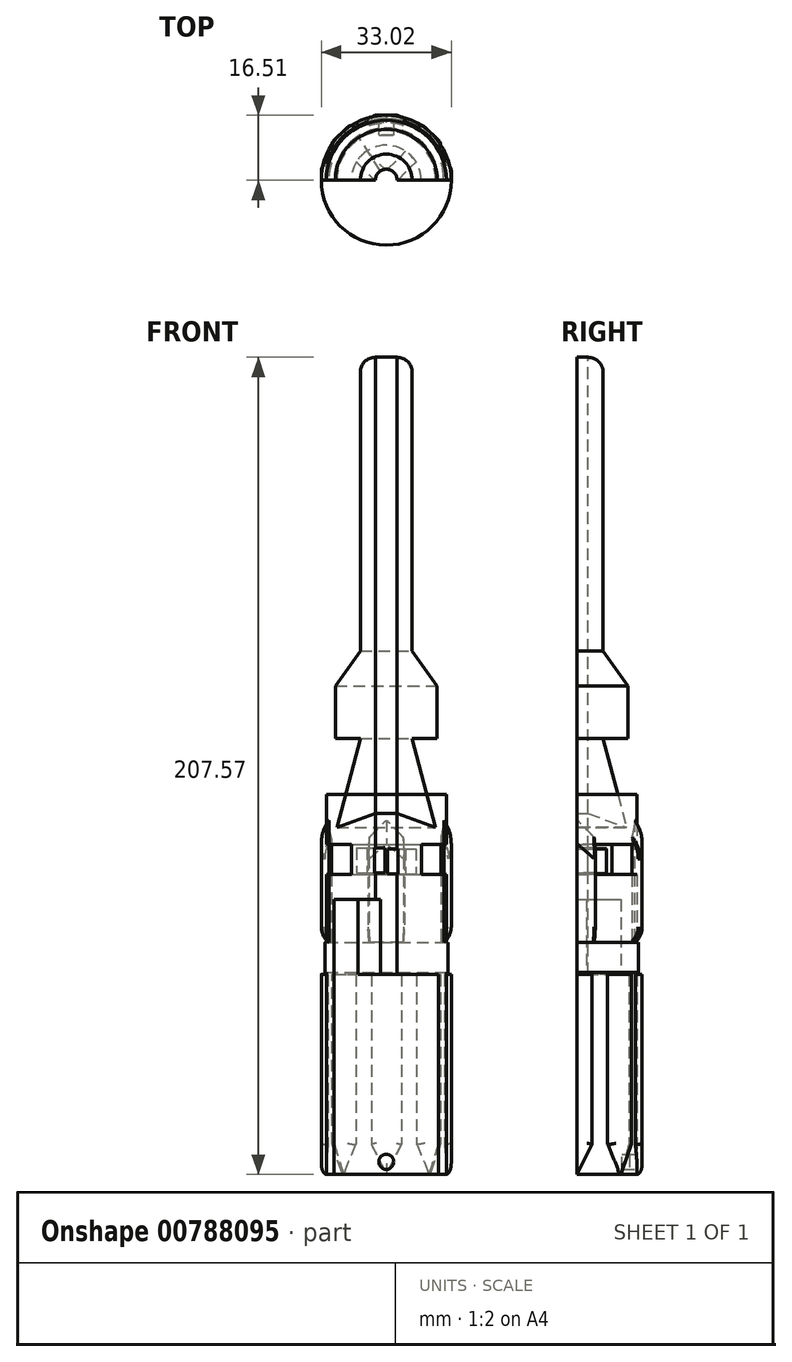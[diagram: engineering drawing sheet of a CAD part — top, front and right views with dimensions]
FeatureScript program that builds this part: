
annotation { "Feature Type Name" : "Feature", "Feature Type Description" : "" }
export const myFeature = defineFeature(function(context is Context, id is Id, definition is map)
    precondition{}
    {
        {
            var Q0;
            Q0=qCreatedBy(makeId("Right.planeOp"),FACE);
            var sketch = newSketch(context, id + "F0", { "sketchPlane" : qUnion([Q0])});
            skLineSegment(sketch, "E0", {"start": v(0, 0) * mm, "end": v(0, 228.6) * mm});
            skLineSegment(sketch, "E1", {"start": v(0, 0) * mm, "end": v(-15.24, 0) * mm});
            skLineSegment(sketch, "E2", {"start": v(-15.24, 0) * mm, "end": v(-15.24, 51.26) * mm});
            skLineSegment(sketch, "E3", {"start": v(-15.24, 76.2) * mm, "end": v(-8.9, 76.2) * mm});
            skLineSegment(sketch, "E4", {"start": v(-8.9, 76.2) * mm, "end": v(-8.9, 83.82) * mm});
            skLineSegment(sketch, "E5", {"start": v(-8.9, 83.82) * mm, "end": v(-15.24, 83.82) * mm});
            skLineSegment(sketch, "E6", {"start": v(-15.24, 83.82) * mm, "end": v(-15.24, 96.52) * mm});
            skLineSegment(sketch, "E7", {"start": v(-15.24, 96.52) * mm, "end": v(-8.9, 96.52) * mm});
            skLineSegment(sketch, "E8", {"start": v(-8.9, 96.52) * mm, "end": v(0, 96.52) * mm});
            skLineSegment(sketch, "E9", {"start": v(-15.24, 51.26) * mm, "end": v(-15.62, 51.26) * mm});
            skLineSegment(sketch, "E10", {"start": v(-15.62, 51.26) * mm, "end": v(-15.62, 58.88) * mm});
            skLineSegment(sketch, "E11", {"start": v(-15.62, 58.88) * mm, "end": v(-15.24, 58.88) * mm});
            skLineSegment(sketch, "E12.trimOffspring", {"start": v(-15.24, 58.88) * mm, "end": v(-15.24, 76.2) * mm});
            skSolve(sketch);
        }
        {
            var Q0;
            {var subQ0=sQuery(id+"F0.wireOp",EDGE,"E1");Q0=makeQuery(id+"F0.imprint","IMPRINT",FACE,{"disambiguationData":[TD([[makeQuery(id+"F0.imprint","IMPRINT",EDGE,{"derivedFrom":subQ0}),-1.0]])]});}
            var Q1;
            Q1=sQuery(id+"F0.wireOp",EDGE,"E0");
            revolve(context, id + "F1", {"surfaceOperationType" : NewSurfaceOperationType.NEW, "entities" : qUnion([Q0]), "axis" : qUnion([Q1]), "revolveType" : RevolveType.FULL});
        }
        {
            var Q0;
            Q0=qCreatedBy(makeId("Front.planeOp"),FACE);
            cPlane(context, id + "F2", {"entities" : qUnion([Q0]), "cplaneType" : CPlaneType.OFFSET, "offset" : 15.24 * mm, "oppositeDirection" : true, "width" : 152.4 * mm, "height" : 152.4 * mm});
        }
        {
            var Q0;
            Q0=qCreatedBy(id+"F2.planeOp",FACE);
            var sketch = newSketch(context, id + "F3", { "sketchPlane" : qUnion([Q0])});
            skLineSegment(sketch, "E13.top", {"start": v(0, 50.8) * mm, "end": v(-3.81, 50.8) * mm});
            skLineSegment(sketch, "E13.right", {"start": v(-3.81, 7.62) * mm, "end": v(-3.81, 50.8) * mm});
            skLineSegment(sketch, "E14.top", {"start": v(0, 50.8) * mm, "end": v(3.8, 50.8) * mm});
            skLineSegment(sketch, "E14.right", {"start": v(3.81, 7.62) * mm, "end": v(3.8, 50.8) * mm});
            skLineSegment(sketch, "E15", {"start": v(3.81, 7.62) * mm, "end": v(0, 0) * mm});
            skLineSegment(sketch, "E16", {"start": v(-3.81, 7.62) * mm, "end": v(0, 0) * mm});
            skSolve(sketch);
        }
        {
            var Q0;
            Q0=makeQuery(id+"F3.imprint","IMPRINT",FACE,{"disambiguationData":[TD([[makeQuery(id+"F3.imprint","IMPRINT",EDGE,{"derivedFrom":sQuery(id+"F3.wireOp",EDGE,"E13.top")}),1.0]])]});
            extrude(context, id + "F4", {"entities" : qUnion([Q0]), "operationType" : NewBodyOperationType.ADD, "oppositeDirection" : true, "depth" : 1.27 * mm, "offsetDistance" : 25.4 * mm, "hasSecondDirection" : true, "secondDirectionOppositeDirection" : false, "secondDirectionDepth" : 6.35 * mm});
        }
        {
            var Q0;
            Q0=makeQuery(id+"F4.opExtrude","CAP_EDGE",EDGE,{"disambiguationData":[OSD([sQuery(id+"F3.wireOp",EDGE,"E13.right")])],"isStart":false});
            var Q1;
            Q1=makeQuery(id+"F4.opExtrude","CAP_EDGE",EDGE,{"disambiguationData":[OSD([sQuery(id+"F3.wireOp",EDGE,"E14.right")])],"isStart":false});
            var Q2;
            Q2=makeQuery(id+"F4.opExtrude","CAP_EDGE",EDGE,{"disambiguationData":[OSD([sQuery(id+"F3.wireOp",EDGE,"E16")])],"isStart":false});
            var Q3;
            Q3=makeQuery(id+"F4.opExtrude","CAP_EDGE",EDGE,{"disambiguationData":[OSD([sQuery(id+"F3.wireOp",EDGE,"E15")])],"isStart":false});
            fillet(context, id + "F5", {"entities" : qUnion([Q0, Q1, Q2, Q3]), "radius" : 1.27 * mm, "tangentPropagation" : true, "allowEdgeOverflow" : false});
        }
        {
            var Q0;
            Q0=qCreatedBy(makeId("Front.planeOp"),FACE);
            var sketch = newSketch(context, id + "F6", { "sketchPlane" : qUnion([Q0])});
            skLineSegment(sketch, "E17", {"start": v(0, 0) * mm, "end": v(0, 228.6) * mm});
            skSolve(sketch);
        }
        {
            var Q0;
            Q0=makeQuery(id+"F1.opRevolve","SWEPT_BODY",BODY,{"disambiguationData":[OSD([sQuery(id+"F0.wireOp",EDGE,"E0"),sQuery(id+"F0.wireOp",EDGE,"E1"),sQuery(id+"F0.wireOp",EDGE,"E2"),sQuery(id+"F0.wireOp",EDGE,"E3"),sQuery(id+"F0.wireOp",EDGE,"E4"),sQuery(id+"F0.wireOp",EDGE,"E5"),sQuery(id+"F0.wireOp",EDGE,"E6"),sQuery(id+"F0.wireOp",EDGE,"E7"),sQuery(id+"F0.wireOp",EDGE,"E8")])]});
            var Q1;
            Q1=sQuery(id+"F6.wireOp",EDGE,"E17");
            circularPattern(context, id + "F7", {"entities" : qUnion([Q0]), "axis" : qUnion([Q1]), "angle" : 360 * degree, "instanceCount" : 8, "equalSpace" : true});
        }
        {
            var Q0;
            Q0=makeQuery(id+"F1.opRevolve","SWEPT_FACE",FACE,{"disambiguationData":[OSD([sQuery(id+"F0.wireOp",EDGE,"E11")])]});
            var sketch = newSketch(context, id + "F8", { "sketchPlane" : qUnion([Q0])});
            skArc(sketch, "E18", {"start": v(15.83, -4.7) * mm, "mid": v(16.5, -0.03) * mm, "end": v(15.85, 4.63) * mm});
            skArc(sketch, "E19.0", {"start": v(13.93, -4.38) * mm, "mid": v(14.6, -0.02) * mm, "end": v(13.94, 4.35) * mm});
            skLineSegment(sketch, "E20", {"start": v(13.93, -4.38) * mm, "end": v(15.83, -4.7) * mm});
            skLineSegment(sketch, "E21", {"start": v(13.94, 4.35) * mm, "end": v(15.85, 4.63) * mm});
            skPoint(sketch, "E22.start.orphan", {"position": v(14.6, 0) * mm});
            skSolve(sketch);
        }
        {
            var Q0;
            Q0=qSketchRegion(id+"F8",true);
            extrude(context, id + "F9", {"entities" : qUnion([Q0]), "depth" : 31.75 * mm, "offsetDistance" : 25.4 * mm});
        }
        {
            var Q0;
            Q0=makeQuery(id+"F9.opExtrude","CAP_EDGE",EDGE,{"disambiguationData":[OSD([sQuery(id+"F8.wireOp",EDGE,"E21")])],"isStart":false});
            var Q1;
            Q1=makeQuery(id+"F9.opExtrude","CAP_EDGE",EDGE,{"disambiguationData":[OSD([sQuery(id+"F8.wireOp",EDGE,"E20")])],"isStart":false});
            chamfer(context, id + "F10", {"entities" : qUnion([Q0, Q1]), "width" : 5.08 * mm, "tangentPropagation" : true});
        }
        {
            var Q0;
            Q0=makeQuery(id+"F10.opChamfer","BLEND_EDGE",EDGE,{"blendedFrom":[makeQuery(id+"F9.opExtrude","CAP_EDGE",EDGE,{"disambiguationData":[OSD([sQuery(id+"F8.wireOp",EDGE,"E20")])],"isStart":false}),makeQuery(id+"F9.opExtrude","SWEPT_FACE",FACE,{"disambiguationData":[OSD([sQuery(id+"F8.wireOp",EDGE,"E18")])]})],"blendedInto":[makeQuery(id+"F9.opExtrude","SWEPT_FACE",FACE,{"disambiguationData":[OSD([sQuery(id+"F8.wireOp",EDGE,"E18")])]})]});
            var Q1;
            Q1=makeQuery(id+"F10.opChamfer","BLEND_EDGE",EDGE,{"blendedFrom":[makeQuery(id+"F9.opExtrude","CAP_EDGE",EDGE,{"disambiguationData":[OSD([sQuery(id+"F8.wireOp",EDGE,"E21")])],"isStart":false}),makeQuery(id+"F9.opExtrude","SWEPT_FACE",FACE,{"disambiguationData":[OSD([sQuery(id+"F8.wireOp",EDGE,"E18")])]})],"blendedInto":[makeQuery(id+"F9.opExtrude","SWEPT_FACE",FACE,{"disambiguationData":[OSD([sQuery(id+"F8.wireOp",EDGE,"E18")])]})]});
            fillet(context, id + "F11", {"entities" : qUnion([Q0, Q1]), "radius" : 5.08 * mm, "tangentPropagation" : true, "allowEdgeOverflow" : false});
        }
        {
            var Q0;
            Q0=makeQuery(id+"F9.opExtrude","CAP_EDGE",EDGE,{"disambiguationData":[OSD([sQuery(id+"F8.wireOp",EDGE,"E18")])],"isStart":true});
            fillet(context, id + "F12", {"entities" : qUnion([Q0]), "radius" : 5.08 * mm, "tangentPropagation" : true, "allowEdgeOverflow" : false});
        }
        {
            var Q0;
            Q0=makeQuery(id+"F12.opFillet","BLEND_EDGE",EDGE,{"blendedFrom":[makeQuery(id+"F9.opExtrude","CAP_EDGE",EDGE,{"disambiguationData":[OSD([sQuery(id+"F8.wireOp",EDGE,"E18")])],"isStart":true}),makeQuery(id+"F9.opExtrude","SWEPT_FACE",FACE,{"disambiguationData":[OSD([sQuery(id+"F8.wireOp",EDGE,"E20")])]})],"blendedInto":[makeQuery(id+"F9.opExtrude","SWEPT_FACE",FACE,{"disambiguationData":[OSD([sQuery(id+"F8.wireOp",EDGE,"E20")])]})]});
            var Q1;
            Q1=makeQuery(id+"F12.opFillet","BLEND_EDGE",EDGE,{"blendedFrom":[makeQuery(id+"F9.opExtrude","CAP_EDGE",EDGE,{"disambiguationData":[OSD([sQuery(id+"F8.wireOp",EDGE,"E18")])],"isStart":true}),makeQuery(id+"F9.opExtrude","SWEPT_FACE",FACE,{"disambiguationData":[OSD([sQuery(id+"F8.wireOp",EDGE,"E21")])]})],"blendedInto":[makeQuery(id+"F9.opExtrude","SWEPT_FACE",FACE,{"disambiguationData":[OSD([sQuery(id+"F8.wireOp",EDGE,"E21")])]})]});
            fillet(context, id + "F13", {"entities" : qUnion([Q0, Q1]), "radius" : 0.38 * mm, "tangentPropagation" : true, "allowEdgeOverflow" : false});
        }
        {
            var Q0;
            Q0=makeQuery(id+"F9.opExtrude","SWEPT_BODY",BODY,{"disambiguationData":[OSD([sQuery(id+"F8.wireOp",EDGE,"E18"),sQuery(id+"F8.wireOp",EDGE,"E19.0"),sQuery(id+"F8.wireOp",EDGE,"E20"),sQuery(id+"F8.wireOp",EDGE,"E21")])]});
            var Q1;
            Q1=sQuery(id+"F6.wireOp",EDGE,"E17");
            circularPattern(context, id + "F14", {"entities" : qUnion([Q0]), "axis" : qUnion([Q1]), "angle" : 360 * degree, "instanceCount" : 4, "equalSpace" : true});
        }
        {
            var Q0;
            Q0=qCreatedBy(makeId("Front.planeOp"),FACE);
            var sketch = newSketch(context, id + "F15", { "sketchPlane" : qUnion([Q0])});
            skLineSegment(sketch, "E23", {"start": v(0, 92.64) * mm, "end": v(0, 207.57) * mm});
            skLineSegment(sketch, "E24", {"start": v(0, 207.57) * mm, "end": v(6.6, 207.57) * mm});
            skLineSegment(sketch, "E25", {"start": v(6.6, 207.57) * mm, "end": v(6.6, 132.9) * mm});
            skLineSegment(sketch, "E26", {"start": v(6.6, 132.9) * mm, "end": v(12.94, 124.1) * mm});
            skLineSegment(sketch, "E27", {"start": v(12.94, 124.1) * mm, "end": v(12.94, 110.74) * mm});
            skLineSegment(sketch, "E28", {"start": v(12.94, 110.74) * mm, "end": v(6.6, 110.74) * mm});
            skLineSegment(sketch, "E29", {"start": v(6.6, 110.74) * mm, "end": v(12.55, 88.13) * mm});
            skLineSegment(sketch, "E30", {"start": v(12.55, 88.13) * mm, "end": v(0, 92.64) * mm});
            skSolve(sketch);
        }
        {
            var Q0;
            Q0=qSketchRegion(id+"F15",true);
            var Q1;
            Q1=sQuery(id+"F6.wireOp",EDGE,"E17");
            revolve(context, id + "F16", {"surfaceOperationType" : NewSurfaceOperationType.NEW, "entities" : qUnion([Q0]), "axis" : qUnion([Q1]), "revolveType" : RevolveType.FULL});
        }
        {
            var Q0;
            Q0=makeQuery(id+"F16.opRevolve","SWEPT_EDGE",EDGE,{"disambiguationData":[OSD([sQuery(id+"F15.wireOp",EDGE,"E24"),sQuery(id+"F15.wireOp",EDGE,"E25")])]});
            fillet(context, id + "F17", {"entities" : qUnion([Q0]), "radius" : 3.8 * mm, "tangentPropagation" : true, "allowEdgeOverflow" : false});
        }
        {
            var Q0;
            Q0=qCreatedBy(makeId("Right.planeOp"),FACE);
            var Q1;
            Q1=sQuery(id+"F6.wireOp",EDGE,"E17");
            cPlane(context, id + "F18", {"entities" : qUnion([Q0, Q1]), "cplaneType" : CPlaneType.LINE_ANGLE, "offset" : 25.4 * mm, "angle" : 45 * degree, "width" : 152.4 * mm, "height" : 152.4 * mm});
        }
        {
            var Q0;
            Q0=qCreatedBy(id+"F18.planeOp",FACE);
            var sketch = newSketch(context, id + "F19", { "sketchPlane" : qUnion([Q0])});
            skLineSegment(sketch, "E31.bottom", {"start": v(2.07, 82.73) * mm, "end": v(-1.74, 82.73) * mm});
            skLineSegment(sketch, "E31.top", {"start": v(2.07, 76.38) * mm, "end": v(-1.74, 76.38) * mm});
            skLineSegment(sketch, "E31.left", {"start": v(2.07, 82.73) * mm, "end": v(2.07, 76.38) * mm});
            skLineSegment(sketch, "E31.right", {"start": v(-1.74, 82.73) * mm, "end": v(-1.74, 76.38) * mm});
            skSolve(sketch);
        }
        {
            var Q0;
            Q0=qSketchRegion(id+"F19",true);
            extrude(context, id + "F20", {"entities" : qUnion([Q0]), "operationType" : NewBodyOperationType.REMOVE, "depth" : 8.9 * mm, "offsetDistance" : 25.4 * mm, "hasSecondDirection" : true, "secondDirectionOppositeDirection" : true, "secondDirectionDepth" : 8.9 * mm});
        }
        {
            var Q0;
            Q0=qCreatedBy(makeId("Front.planeOp"),FACE);
            var Q1;
            Q1=sQuery(id+"F6.wireOp",EDGE,"E17");
            cPlane(context, id + "F21", {"entities" : qUnion([Q0, Q1]), "cplaneType" : CPlaneType.LINE_ANGLE, "offset" : 25.4 * mm, "angle" : 225 * degree, "width" : 152.4 * mm, "height" : 152.4 * mm});
        }
        {
            var Q0;
            Q0=qCreatedBy(id+"F21.planeOp",FACE);
            var sketch = newSketch(context, id + "F22", { "sketchPlane" : qUnion([Q0])});
            skLineSegment(sketch, "E32.bottom", {"start": v(-2.08, 82.92) * mm, "end": v(1.73, 82.92) * mm});
            skLineSegment(sketch, "E32.top", {"start": v(-2.08, 76.57) * mm, "end": v(1.73, 76.57) * mm});
            skLineSegment(sketch, "E32.left", {"start": v(-2.08, 82.92) * mm, "end": v(-2.08, 76.57) * mm});
            skLineSegment(sketch, "E32.right", {"start": v(1.73, 82.92) * mm, "end": v(1.73, 76.57) * mm});
            skSolve(sketch);
        }
        {
            var Q0;
            Q0=qSketchRegion(id+"F22",true);
            extrude(context, id + "F23", {"entities" : qUnion([Q0]), "operationType" : NewBodyOperationType.REMOVE, "oppositeDirection" : true, "depth" : 25.4 * mm, "offsetDistance" : 25.4 * mm, "hasSecondDirection" : true, "secondDirectionOppositeDirection" : false, "secondDirectionDepth" : 25.4 * mm});
        }
        {
            var Q0;
            Q0=makeQuery(id+"F1.opRevolve","SWEPT_FACE",FACE,{"disambiguationData":[OSD([sQuery(id+"F0.wireOp",EDGE,"E1")])]});
            var sketch = newSketch(context, id + "F24", { "sketchPlane" : qUnion([Q0])});
            skCircle(sketch, "E33", {"center": v(0, 0) * mm, "radius": 15.16 * mm});
            skCircle(sketch, "E34.0", {"center": v(0, 0) * mm, "radius": 13.25 * mm});
            skSolve(sketch);
        }
        {
            var Q0;
            Q0=makeQuery(id+"F24.imprint","IMPRINT",FACE,{"disambiguationData":[TD([[makeQuery(id+"F24.imprint","IMPRINT",EDGE,{"derivedFrom":sQuery(id+"F24.wireOp",EDGE,"E34.0")}),1.0]])]});
            extrude(context, id + "F25", {"entities" : qUnion([Q0]), "operationType" : NewBodyOperationType.REMOVE, "oppositeDirection" : true, "depth" : 50.8 * mm, "offsetDistance" : 25.4 * mm});
        }
        {
            var Q0;
            Q0=makeQuery(id+"F16.opRevolve","SWEPT_FACE",FACE,{"disambiguationData":[OSD([sQuery(id+"F15.wireOp",EDGE,"E24")])]});
            extrude(context, id + "F26", {"entities" : qUnion([Q0]), "operationType" : NewBodyOperationType.REMOVE, "oppositeDirection" : true, "depth" : 190.5 * mm, "offsetDistance" : 25.4 * mm});
        }
        {
            var Q0;
            Q0=makeQuery(id+"F25.boolean.opBoolean","COPY",FACE,{"disambiguationData":[OD(0.0)],"derivedFrom":makeQuery(id+"F25.opExtrude","CAP_FACE",FACE,{"disambiguationData":[OSD([sQuery(id+"F24.wireOp",EDGE,"E34.0")])],"isStart":false})});
            var sketch = newSketch(context, id + "F27", { "sketchPlane" : qUnion([Q0])});
            skLineSegment(sketch, "E35", {"start": v(-1.46, -2.37) * mm, "end": v(-7.12, -11.18) * mm});
            skLineSegment(sketch, "E36", {"start": v(1.57, 2.3) * mm, "end": v(7.24, 11.1) * mm});
            skLineSegment(sketch, "E37", {"start": v(7.24, 11.1) * mm, "end": v(1.57, 2.3) * mm});
            skLineSegment(sketch, "E38", {"start": v(1.46, -2.37) * mm, "end": v(3.3, -12.84) * mm});
            skLineSegment(sketch, "E39", {"start": v(-1.57, 2.3) * mm, "end": v(-4.84, 12.34) * mm});
            skSolve(sketch);
        }
        {
            var Q0;
            {var subQ0=sQuery(id+"F27.wireOp",EDGE,"E35");Q0=makeQuery(id+"F27.imprint","IMPRINT",FACE,{"disambiguationData":[TD([[makeQuery(id+"F27.imprint","IMPRINT",EDGE,{"derivedFrom":subQ0}),-1.0]])]});}
            var Q1;
            {var subQ0=sQuery(id+"F27.wireOp",EDGE,"E37");Q1=makeQuery(id+"F27.imprint","IMPRINT",FACE,{"disambiguationData":[TD([[makeQuery(id+"F27.imprint","IMPRINT",EDGE,{"derivedFrom":subQ0}),1.0]])]});}
            extrude(context, id + "F28", {"entities" : qUnion([Q0, Q1]), "operationType" : NewBodyOperationType.REMOVE, "oppositeDirection" : true, "depth" : 19.05 * mm, "offsetDistance" : 25.4 * mm});
        }
        {
            var Q0;
            Q0=qCreatedBy(id+"F2.planeOp",FACE);
            var sketch = newSketch(context, id + "F29", { "sketchPlane" : qUnion([Q0])});
            skCircle(sketch, "E40", {"center": v(0, 3.18) * mm, "radius": 1.9 * mm});
            skLineSegment(sketch, "E41", {"start": v(0, 1.27) * mm, "end": v(0, 0) * mm});
            skSolve(sketch);
        }
        {
            var Q0;
            Q0=qSketchRegion(id+"F29",true);
            extrude(context, id + "F30", {"entities" : qUnion([Q0]), "depth" : 3.8 * mm, "offsetDistance" : 25.4 * mm});
        }
        {
            var Q0;
            Q0=makeQuery(id+"F30.opExtrude","SWEPT_BODY",BODY,{"disambiguationData":[OSD([sQuery(id+"F29.wireOp",EDGE,"E40")])]});
            var Q1;
            Q1=qCreatedBy(makeId("Front.planeOp"),FACE);
            mirror(context, id + "F31", {"entities" : qUnion([Q0]), "mirrorPlane" : qUnion([Q1])});
        }
        {
            var Q0;
            Q0=makeQuery(id+"F30.opExtrude","CAP_EDGE",EDGE,{"disambiguationData":[OSD([sQuery(id+"F29.wireOp",EDGE,"E40")])],"isStart":false});
            var Q1;
            Q1=makeQuery(id+"F31.opPattern","COPY",EDGE,{"derivedFrom":makeQuery(id+"F30.opExtrude","CAP_EDGE",EDGE,{"disambiguationData":[OSD([sQuery(id+"F29.wireOp",EDGE,"E40")])],"isStart":false}),"instanceName":"1"});
            fillet(context, id + "F32", {"entities" : qUnion([Q0, Q1]), "radius" : 0.13 * mm, "tangentPropagation" : true, "allowEdgeOverflow" : false});
        }
        {
            var Q0;
            Q0=qCreatedBy(makeId("Front.planeOp"),FACE);
            var sketch = newSketch(context, id + "F33", { "sketchPlane" : qUnion([Q0])});
            skLineSegment(sketch, "E42.bottom", {"start": v(-40.3, 243.95) * mm, "end": v(51.3, 243.95) * mm});
            skLineSegment(sketch, "E42.top", {"start": v(-40.3, -22.5) * mm, "end": v(51.3, -22.5) * mm});
            skLineSegment(sketch, "E42.left", {"start": v(-40.3, 243.95) * mm, "end": v(-40.3, -22.5) * mm});
            skLineSegment(sketch, "E42.right", {"start": v(51.3, 243.95) * mm, "end": v(51.3, -22.5) * mm});
            skSolve(sketch);
        }
        {
            var Q0;
            Q0 = qSketchRegion(id + "F33", true);
            extrude(context, id + "F34", {"entities" : qUnion([Q0]), "operationType" : NewBodyOperationType.REMOVE, "depth" : 25.4 * mm, "offsetDistance" : 25.4 * mm});
        }
    });
